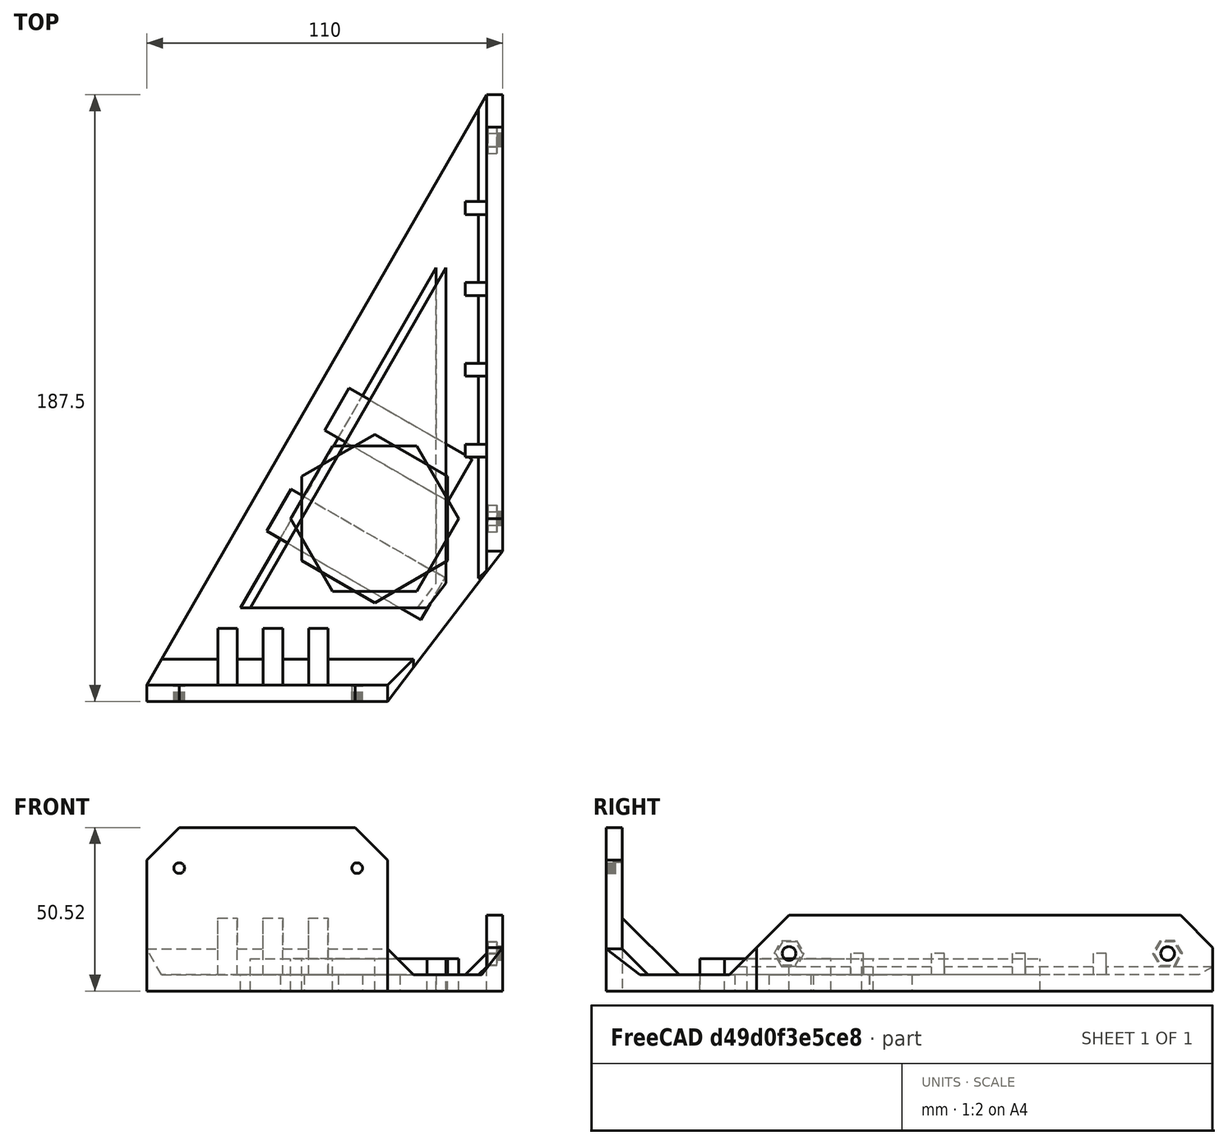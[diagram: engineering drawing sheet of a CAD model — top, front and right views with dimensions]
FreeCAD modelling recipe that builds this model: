
FCSTD DOCUMENT  (FreeCAD 0.18R14555 (Git shallow))
Label: mk3s-bracket-trim-down
License: All rights reserved
LicenseURL: http://en.wikipedia.org/wiki/All_rights_reserved
objects: Part::Feature×5, Sketcher::SketchObject×2, PartDesign::Pad×2, PartDesign::Body×2, Part::Box×2, Mesh::Feature×1, Part::Cut×1, Part::MultiFuse×1
note: 17 computed .brp shape members not serialized (recipe doc carries the construction recipe); baked Part::Feature solids carry a one-line shape summary decoded from their .brp

FEATURE [Mesh::Feature] PSU_brace_1_  label="PSU_brace(1)"
  Placement = pos=(-165,-131,0) rot=(0,0,1;0rad)
FEATURE [Part::Feature] PSU_brace_1_001
  shape: bbox 110 x 187.5 x 50.52 mm, 850 faces, 0 solids (baked)
FEATURE [Part::Feature] PSU_brace_1_001001  label="PSU_brace_1_002"
  shape: bbox 110 x 187.5 x 50.52 mm, 240 faces, 0 solids (baked)
FEATURE [Part::Feature] PSU_brace_1_001001_solid  label="PSU_brace_1_002 (Solid)"
  Placement = pos=(0,0,-220) rot=(0,0,1;0rad)
  shape: bbox 110 x 187.5 x 50.52 mm, 240 faces (baked)
FEATURE [Sketcher::SketchObject] Sketch
  MapMode = 5
  Support = -> [XY_Plane]
  sketch-geometry (7):
    g0: LineSegment StartX=0 StartY=-26 StartZ=0 EndX=22.5167 EndY=-13 EndZ=0
    g1: LineSegment StartX=22.5167 StartY=-13 StartZ=0 EndX=22.5167 EndY=13 EndZ=0
    g2: LineSegment StartX=22.5167 StartY=13 StartZ=0 EndX=3.6e-15 EndY=26 EndZ=0
    g3: LineSegment StartX=3.6e-15 StartY=26 StartZ=0 EndX=-22.5167 EndY=13 EndZ=0
    g4: LineSegment StartX=-22.5167 StartY=13 StartZ=0 EndX=-22.5167 EndY=-13 EndZ=0
    g5: LineSegment StartX=-22.5167 StartY=-13 StartZ=0 EndX=0 EndY=-26 EndZ=0
    g6: Circle [constr] CenterX=0 CenterY=0 CenterZ=0 NormalX=0 NormalY=0 NormalZ=1 AngleXU=0 Radius=26
  constraints (15):
    c: Coincident(g0,g1)
    c: Coincident(g1,g2)
    c: Coincident(g2,g3)
    c: Coincident(g3,g4)
    c: Coincident(g4,g5)
    c: Coincident(g5,g0)
    c: Equal(g0, g1-g5) x5
    c: PointOnObject(g0,g6)
    c: PointOnObject(g1,g6)
    c: PointOnObject(g2,g6)
    c: PointOnObject(g3,g6)
    c: PointOnObject(g4,g6)
    c: PointOnObject(g5,g6)
    c: Coincident(g6,g-1)
    c: PointOnObject(g5,g-2)
FEATURE [PartDesign::Pad] Pad
  Length = 10
  Length2 = 100
  Profile = -> Sketch
  Type = 0
FEATURE [PartDesign::Body] Body
  Group = -> [Sketch,Pad]
  Origin = -> Origin
  Tip = -> Pad
FEATURE [Part::Feature] Body001
  Placement = pos=(0,0,0) rot=(0,0,1;5.75959rad)
  shape: bbox 52 x 45.03 x 10 mm, 8 faces (baked)
FEATURE [Sketcher::SketchObject] Sketch001
  MapMode = 5
  Support = -> [XY_Plane001]
  sketch-geometry (4):
    g0: LineSegment StartX=-38.4636 StartY=-27.5414 StartZ=0 EndX=16.2258 EndY=-27.5414 EndZ=0
    g1: LineSegment StartX=-38.4636 StartY=-27.5414 StartZ=0 EndX=22 EndY=77.5657 EndZ=0
    g2: LineSegment StartX=16.2258 StartY=-27.5414 StartZ=0 EndX=22 EndY=-20 EndZ=0
    g3: LineSegment StartX=22 StartY=-20 StartZ=0 EndX=22 EndY=77.5657 EndZ=0
  constraints (10):
    c: Horizontal(g0)
    c: Coincident(g1,g0)
    c: Angle(g0,g1) = 1.04877
    c: Coincident(g2,g0)
    c: Angle(g2,g0) = 2.22425
    c: DistanceY(g2,g-1) = 20
    c: DistanceX(g-1,g2) = 22
    c: Coincident(g3,g2)
    c: Vertical(g3)
    c: Coincident(g1,g3)
FEATURE [PartDesign::Pad] Pad001
  Length = 10
  Length2 = 100
  Profile = -> Sketch001
  Type = 0
FEATURE [PartDesign::Body] Body002
  Group = -> [Sketch001,Pad001]
  Origin = -> Origin001
  Tip = -> Pad001
FEATURE [Part::Feature] Body002001  label="Body003"
  Placement = pos=(-3,0,-24) rot=(0,0,1;0rad)
  shape: bbox 60.46 x 105.1 x 10 mm, 6 faces (baked)
FEATURE [Part::Cut] Cut
  Base = -> PSU_brace_1_001001_solid
  Placement = pos=(0,0,20.56) rot=(0,0,1;0rad)
  Tool = -> Body002001
FEATURE [Part::Box] Box  label="Cube"
  AttacherType = Attacher::AttachEngine3D
  Height = 5
  Length = 55
  Placement = pos=(-33.3773,-3.86712,0) rot=(0,0,1;5.76098rad)
  Width = 15
FEATURE [Part::Box] Box001  label="Cube001"
  AttacherType = Attacher::AttachEngine3D
  Height = 5
  Length = 44
  Placement = pos=(-15.4209,27.3349,0) rot=(0,0,-1;0.522203rad)
  Width = 15
FEATURE [Part::MultiFuse] Fusion
  Shapes = -> [Cut,Box,Box001]
